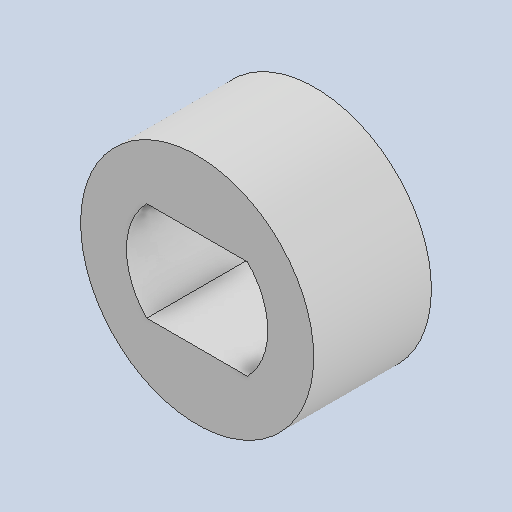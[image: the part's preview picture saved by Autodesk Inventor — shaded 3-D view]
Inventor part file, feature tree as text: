
AUTODESK INVENTOR PART (.ipt)
format: ipt  version: 2022 (Build 260153070, 153G)  size: 103,936 bytes
history: native  units: in
note: dims shown in document units (in); Inventor stores cm internally (conversion verified against a paired STEP export)
features: other x3, sketch x1, plane x1
ambient origin geometry x8: Origin, YZ Plane, XZ Plane, XY Plane, X Axis, Y Axis, Z Axis, Center Point
bodies: Solid1 (feature_tree)
feature tree (5):
  other  "TTencoderspacer.ipt"
  other  "Solid1::TTencoderspacer.ipt"
  other  "TaggingFeature1"
  sketch  "Sketch1"  dims[d0=0.3937in]
  plane  "Work Plane1"
